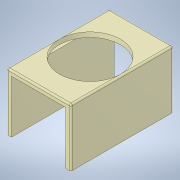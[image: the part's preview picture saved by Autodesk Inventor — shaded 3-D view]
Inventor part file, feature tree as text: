
AUTODESK INVENTOR PART (.ipt)
format: ipt  version: 2022 (Build 260153000, 153)  size: 138,240 bytes
history: native  units: in
note: dims shown in document units (in); Inventor stores cm internally (conversion verified against a paired STEP export)
features: other x2, sketch x2, extrude x1, fillet x1, hole x1
ambient origin geometry x8: Origin, YZ Plane, XZ Plane, XY Plane, X Axis, Y Axis, Z Axis, Center Point
bodies: Solid1 (feature_tree)
feature tree (7):
  other  "Annotations"
  extrude  "Extrusion1"  Depth=2.5in
  fillet  "Fillet1"  Radius=0.1875in
  hole  "Hole1"  [1 undecoded]
  sketch  "Sketch1"  dims[d0=2.25in d1=2.5in d2=0.1875in]
  sketch  "Sketch2"  dims[d3=0.1875in d4=0.1875in d5=4.0in d6=0.0in d7=0.0625in d8=2.0in d9=1.25in d10=2.375in d11=0.6099in d12=0.0246in d13=2.1886in d14=0.375in d15=0.25in d16=0.5635in d17=0.1875in d18=0.0in]
  other  "General Note 1"
note: 1 required parameter value undecoded (feature->parameter linkage not recoverable at this tier; creation-order binding heuristic only, values carry confidence <= 0.55)
